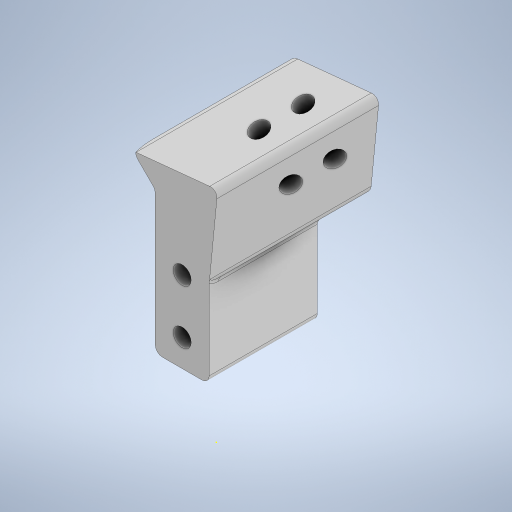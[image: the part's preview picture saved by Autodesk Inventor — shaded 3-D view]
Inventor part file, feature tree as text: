
AUTODESK INVENTOR PART (.ipt)
format: ipt  version: 2024.3 (Build 283343000, 343)  size: 428,032 bytes
history: native  units: mm
features: sketch x15, extrude x11, projected_geometry x7, hole x3, other x1, fillet x1
ambient origin geometry x8: Origin, YZ Plane, XZ Plane, XY Plane, X Axis, Y Axis, Z Axis, Center Point
bodies: Body1 (feature_tree)
feature tree (38):
  other  "ソリッド1"
  extrude  "押し出し1"  Depth=60.0mm
  hole  "穴1"  [1 undecoded]
  extrude  "押し出し2"  Depth=30.0mm TaperAngle=0.0deg
  extrude  "押し出し11"  Depth=7.5mm
  extrude  "押し出し12"  Depth=7.5mm
  extrude  "押し出し17"  Depth=10.5mm
  extrude  "押し出し18"  Depth=10.5mm
  sketch  "スケッチ27"
  extrude  "押し出し19"  Depth=15.0mm
  hole  "穴4"  [1 undecoded]
  hole  "穴5"  [1 undecoded]
  extrude  "押し出し22"  Depth=26.0mm
  extrude  "押し出し23"  Depth=7.5mm
  fillet  "フィレット2"  Radius=7.5mm
  extrude  "押し出し24"  Depth=7.5mm
  extrude  "押し出し25"  Depth=30.0mm
  sketch  "スケッチ1"
  sketch  "スケッチ2"
  sketch  "スケッチ3"
  projected_geometry  "投影ループ1"
  sketch  "スケッチ15"
  projected_geometry  "投影ループ10"
  sketch  "スケッチ16"
  projected_geometry  "投影ループ11"
  sketch  "スケッチ25"
  projected_geometry  "投影ループ18"
  sketch  "スケッチ26"
  projected_geometry  "投影ループ19"
  sketch  "スケッチ28"
  sketch  "スケッチ29"
  sketch  "スケッチ30"
  sketch  "スケッチ33"
  sketch  "スケッチ34"
  projected_geometry  "投影ループ22"
  sketch  "スケッチ35"
  projected_geometry  "投影ループ23"
  sketch  "スケッチ36"
note: 3 required parameter values undecoded (feature->parameter linkage not recoverable at this tier; creation-order binding heuristic only, values carry confidence <= 0.55)
